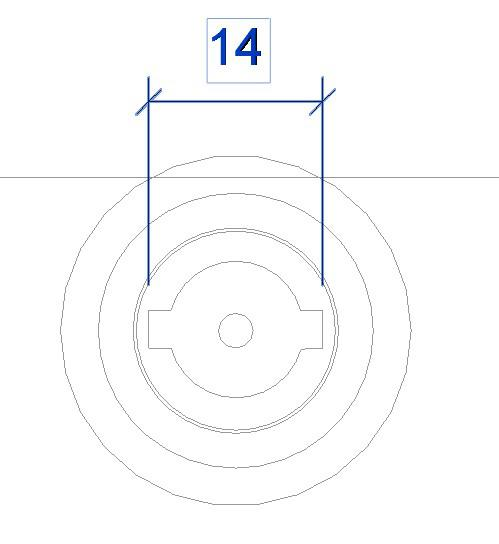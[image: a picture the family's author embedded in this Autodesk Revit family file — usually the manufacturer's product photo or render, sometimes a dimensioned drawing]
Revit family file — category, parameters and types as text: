
# Revit family: AquaMaster-Inverter-P_ENG-RFA-2022
name_source: partatom
category: Mechanické zařízení
units: mm (PartAtom-declared; Revit-internal decimal feet)

## family parameters
Bod výpočtu místnosti = Ne
Kóta kulaté spojky = Použít průměr
Nadpis OmniClass = Climate Control (HVAC)
Ořezat dutým tvarem při načtení = Ne
Sdílené = Ne
Typ dílu = Normální
Vždy vertikální = Ano
Zachovat orientaci poznámky = Ne
Založené na pracovní rovině = Ne
Číslo OmniClass = 23.75.00.00

## types (5) — shared parameters
CI_hot water – inlet = 1'' (OD)
CO_hot water – outlet = 1'' (OD)
MT_CI diameter = 28 mm  [stored 0.0918635 ft]
MT_CO diameter = 28 mm  [stored 0.0918635 ft]
MT_EC1 offset_X = 25 mm  [stored 0.082021 ft]
MT_active power = 0 W
MT_angle length_X = 406 mm  [stored 1.33202 ft]
MT_angle offset = 60 mm  [stored 0.19685 ft]
MT_apparent power = 0 VA
MT_case mat = MT_RAL7016
MT_case width = 526 mm  [stored 1.72572 ft]
MT_clearance back = 200 mm  [stored 0.656168 ft]
MT_clearance front = 600 mm
MT_cover front_X = 446 mm  [stored 1.46325 ft]
MT_cover top_X = 446 mm  [stored 1.46325 ft]
MT_frequency (Hz) = 50 Hz
MT_ground height = 30 mm  [stored 0.0984252 ft]
MT_pipe connector mat = MT_RGB-130-130-130
MT_pipe mat = MT_angle-corner
Popis = Ground-to-water heat pump (R290)
URL = https://www.mastertherm.eu
Výrobce = Master Therm
zero-valued in all types: Cena, MT_CosPhi, Výchozí výška

## per-type parameters (varying)
- AQ45IP: EI_brine – inlet=5/4'' (OD); EO_brine – outlet=5/4'' (OD); El. connection=2xPG16; 4xPG13.5; Komentáře k typům=COMPRESSOR: BLDC Inverter; 15 – 120 rps; oil – (HAF68D1U) – 2.0 l; max. op. current – 24 A; EVAPORATOR: PHE; AISI316; water flow (W/W) – 2.14 kg/s; min. flow – 1.61 kg/s; brine flow (B/W) – 1.04 kg/s; min. flow – 0.63 kg/s; temp. difference – 3 K; int. volume – 5.1 l; pump ext. head – 15 m; pump motor – 400 W; CONDENSER: PHE; AISI316; water flow – 0.7 kg/s; min. flow – 0.53 kg/s; temp. difference – 5 K; int. volume – 4.1 l; pump ext. head – 8.0 m; pump motor – 200 W; REFRIGERANT CIRCUIT: R290 (0.9 kg); AUX. HEATER (optional): není k dispozici; CONTROLS: controller – pCO5; EEV – yes; water probe – yes; mixing probe/output – yes (2x); SHW probe/output – yes; outdoor probe – yes; dynamic set point – yes; refrigerant probe – 2xPT; POWER SUPPLY: 3x400 V; 50 Hz; max. current – 25 A; DIMENSIONS: hot water, brine – 1", 5/4" (OD); 120x53x72 cm; 180 kg; LIMITS: max. water overpress. – 0.25 MPa; max. refr. overpress. – 3.1 MPa; brine min./max.: -5/+20 °C; water min./max.: 20/75 °C; MT_CI offset_X=73 mm  [stored 0.239501 ft]; MT_CO offset_X=173 mm  [stored 0.567585 ft]; MT_EC1 offset_Y=90 mm; MT_EC2 offset_X=25 mm  [stored 0.082021 ft]; MT_EC2 offset_Y=60 mm  [stored 0.19685 ft]; MT_EC3 offset_X=25 mm  [stored 0.082021 ft]; MT_EC3 offset_Y=30 mm  [stored 0.0984252 ft]; MT_EC4 offset_X=421 mm  [stored 1.38123 ft]; MT_EC4 offset_Y=90 mm; MT_EC5 offset_X=421 mm  [stored 1.38123 ft]; MT_EC5 offset_Y=60 mm  [stored 0.19685 ft]; MT_EC5-EC6_YES=Ano; MT_EC6 offset_X=421 mm  [stored 1.38123 ft]; MT_EC6 offset_Y=30 mm  [stored 0.0984252 ft]; MT_EI diameter=35 mm  [stored 0.114829 ft]; MT_EI offset_X=373 mm  [stored 1.22375 ft]; MT_EO diameter=35 mm  [stored 0.114829 ft]; MT_EO offset_X=273 mm  [stored 0.895669 ft]; MT_TYPE=45; MT_angle length_Y=596 mm; MT_angle length_Z=1080 mm; MT_case depth=716 mm; MT_case height=1200 mm; MT_center lock_YES=Ne; MT_clearance left=400 mm  [stored 1.31234 ft]; MT_clearance right=400 mm  [stored 1.31234 ft]; MT_clearance top=1800 mm  [stored 5.90551 ft]; MT_cover front_Y=1120 mm; MT_cover side_X=636 mm; MT_cover side_Y=1120 mm; MT_cover top_Y=636 mm; MT_max. current, incl. aux. heater (A)=25 A; MT_pipe connector angle=0.00°; MT_pipe connector offset=486 mm; MT_pipe connector_X=446 mm  [stored 1.46325 ft]; MT_pipe connector_Y=120 mm  [stored 0.393701 ft]; MT_pivot offset=0 mm  [stored 0 ft]; MT_vent grille_YES=Ne; MT_voltage (V)=400 V; MT_weight (kg)=180; Model=AquaMaster 45 Inverter P
- AQ17IP: EI_brine – inlet=1'' (OD); EO_brine – outlet=1'' (OD); El. connection=4xPG16; Komentáře k typům=COMPRESSOR: BLDC Inverter; 20 – 60 rps; oil – (RFL68EP) – 0.74 l; max. op. current – 12 A; EVAPORATOR: PHE; AISI316; water flow (W/W) – 0.22 kg/s; min. flow – 0.17 kg/s; brine flow (B/W) – 0.18 kg/s; min. flow – 0.11 kg/s; temp. difference – 3 K; int. volume – 2.0 l; pump ext. head – 6.0 m; pump motor – 70 W; CONDENSER: PHE; AISI316; water flow – 0.12 kg/s; min. flow – 0.06 kg/s; temp. difference – 5 K; int. volume – 2.0 l; pump ext. head – 5.0 m; pump motor – 70 W; REFRIGERANT CIRCUIT: R290 (0.152 kg); AUX. HEATER (optional): not available; CONTROLS: controller – pCO5; EEV – yes; water probe – yes; mixing probe/output – yes (2x); SHW probe/output – yes; outdoor probe – yes; dynamic set point – yes; refrigerant probe – 2xPT; POWER SUPPLY: 1x230 V; 50 Hz; max. current – 16 A; DIMENSIONS: hot water, brine – 1", 1" (OD); 84x53x53 cm; 75 kg; LIMITS: max. water overpress. – 0.25 MPa; max. refr. overpress. – 3.1 MPa; brine min./max.: -5/+20 °C; water min./max.: 20/75 °C; MT_CI offset_X=430 mm; MT_CO offset_X=700 mm; MT_EC1 offset_Y=500 mm  [stored 1.64042 ft]; MT_EC2 offset_X=55 mm  [stored 0.180446 ft]; MT_EC2 offset_Y=500 mm  [stored 1.64042 ft]; MT_EC3 offset_X=85 mm  [stored 0.278871 ft]; MT_EC3 offset_Y=500 mm  [stored 1.64042 ft]; MT_EC4 offset_X=115 mm; MT_EC4 offset_Y=500 mm  [stored 1.64042 ft]; MT_EC5 offset_X=115 mm; MT_EC5 offset_Y=500 mm  [stored 1.64042 ft]; MT_EC5-EC6_YES=Ne; MT_EC6 offset_X=115 mm; MT_EC6 offset_Y=500 mm  [stored 1.64042 ft]; MT_EI diameter=28 mm  [stored 0.0918635 ft]; MT_EI offset_X=330 mm; MT_EO diameter=28 mm  [stored 0.0918635 ft]; MT_EO offset_X=60 mm  [stored 0.19685 ft]; MT_TYPE=17; MT_angle length_Y=406 mm  [stored 1.33202 ft]; MT_angle length_Z=720 mm  [stored 2.3622 ft]; MT_case depth=526 mm  [stored 1.72572 ft]; MT_case height=840 mm  [stored 2.75591 ft]; MT_center lock_YES=Ano; MT_clearance left=200 mm  [stored 0.656168 ft]; MT_clearance right=600 mm; MT_clearance top=1440 mm  [stored 4.72441 ft]; MT_cover front_Y=760 mm  [stored 2.49344 ft]; MT_cover side_X=446 mm  [stored 1.46325 ft]; MT_cover side_Y=760 mm  [stored 2.49344 ft]; MT_cover top_Y=446 mm  [stored 1.46325 ft]; MT_max. current, incl. aux. heater (A)=16 A; MT_pipe connector angle=90.00°; MT_pipe connector offset=800 mm; MT_pipe connector_X=760 mm  [stored 2.49344 ft]; MT_pipe connector_Y=85 mm  [stored 0.278871 ft]; MT_pivot offset=526 mm  [stored 1.72572 ft]; MT_vent grille_YES=Ano; MT_voltage (V)=230 V; MT_weight (kg)=75; Model=AquaMaster 17 Inverter P
- AQ22IP: EI_brine – inlet=1'' (OD); EO_brine – outlet=1'' (OD); El. connection=4xPG16; Komentáře k typům=COMPRESSOR: BLDC Inverter; 20 – 90 rps; oil – (RFL68EP) – 0.74 l; max. op. current – 12 A; EVAPORATOR: PHE; AISI316; water flow (W/W) – 0.46 kg/s; min. flow – 0.35 kg/s; brine flow (B/W) – 0.36 kg/s; min. flow – 0.21 kg/s; temp. difference – 3 K; int. volume – 2.0 l; pump ext. head – 4.5 m; pump motor – 70 W; CONDENSER: PHE; AISI316; water flow – 0.25 kg/s; min. flow – 0.13 kg/s; temp. difference – 5 K; int. volume – 2.0 l; pump ext. head – 7.0 m; pump motor – 70 W; REFRIGERANT CIRCUIT: R290 (0.220 kg); AUX. HEATER (optional): není k dispozici; CONTROLS: controller – pCO5; EEV – yes; water probe – yes; mixing probe/output – yes (2x); SHW probe/output – yes; outdoor probe – yes; dynamic set point – yes; refrigerant probe – 2xPT; POWER SUPPLY: 1x230 V; 50 Hz; max. current – 20 A; DIMENSIONS: hot water, brine – 1", 1" (OD); 84x53x53 cm; 80 kg; LIMITS: max. water overpress. – 0.25 MPa; max. refr. overpress. – 3.1 MPa; brine min./max.: -5/+20 °C; water min./max.: 20/75 °C; MT_CI offset_X=430 mm; MT_CO offset_X=700 mm; MT_EC1 offset_Y=500 mm  [stored 1.64042 ft]; MT_EC2 offset_X=55 mm  [stored 0.180446 ft]; MT_EC2 offset_Y=500 mm  [stored 1.64042 ft]; MT_EC3 offset_X=85 mm  [stored 0.278871 ft]; MT_EC3 offset_Y=500 mm  [stored 1.64042 ft]; MT_EC4 offset_X=115 mm; MT_EC4 offset_Y=500 mm  [stored 1.64042 ft]; MT_EC5 offset_X=115 mm; MT_EC5 offset_Y=500 mm  [stored 1.64042 ft]; MT_EC5-EC6_YES=Ne; MT_EC6 offset_X=115 mm; MT_EC6 offset_Y=500 mm  [stored 1.64042 ft]; MT_EI diameter=28 mm  [stored 0.0918635 ft]; MT_EI offset_X=330 mm; MT_EO diameter=28 mm  [stored 0.0918635 ft]; MT_EO offset_X=60 mm  [stored 0.19685 ft]; MT_TYPE=22; MT_angle length_Y=406 mm  [stored 1.33202 ft]; MT_angle length_Z=720 mm  [stored 2.3622 ft]; MT_case depth=526 mm  [stored 1.72572 ft]; MT_case height=840 mm  [stored 2.75591 ft]; MT_center lock_YES=Ano; MT_clearance left=200 mm  [stored 0.656168 ft]; MT_clearance right=600 mm; MT_clearance top=1440 mm  [stored 4.72441 ft]; MT_cover front_Y=760 mm  [stored 2.49344 ft]; MT_cover side_X=446 mm  [stored 1.46325 ft]; MT_cover side_Y=760 mm  [stored 2.49344 ft]; MT_cover top_Y=446 mm  [stored 1.46325 ft]; MT_max. current, incl. aux. heater (A)=20 A; MT_pipe connector angle=90.00°; MT_pipe connector offset=800 mm; MT_pipe connector_X=760 mm  [stored 2.49344 ft]; MT_pipe connector_Y=85 mm  [stored 0.278871 ft]; MT_pivot offset=526 mm  [stored 1.72572 ft]; MT_vent grille_YES=Ano; MT_voltage (V)=230 V; MT_weight (kg)=80; Model=AquaMaster 22 Inverter P
- AQ30IP: EI_brine – inlet=1'' (OD); EO_brine – outlet=1'' (OD); El. connection=2xPG16; 4xPG13.5; Komentáře k typům=COMPRESSOR: BLDC Inverter; 15 – 110 rps; oil – (PZ68S) – 0.75 l; max. op. current – ; EVAPORATOR: PHE; AISI316; water flow (W/W) – 0.99 kg/s; min. flow – 0.74 kg/s; brine flow (B/W) – 0.48 kg/s; min. flow – 0.29 kg/s; temp. difference – 3 K; int. volume – 3.8 l; pump ext. head – 5.5 m; pump motor – 70 W; CONDENSER: PHE; AISI316; water flow – 0.37 kg/s; min. flow – 0.25 kg/s; temp. difference – 5 K; int. volume – 4.0 l; pump ext. head – 6.5 m; pump motor – 70 W; REFRIGERANT CIRCUIT: R290 (0.7 kg); AUX. HEATER (optional): není k dispozici; CONTROLS: controller – pCO5; EEV – yes; water probe – yes; mixing probe/output – yes (2x); SHW probe/output – yes; outdoor probe – yes; dynamic set point – yes; refrigerant probe – 2xPT; POWER SUPPLY: 1x230 V; 50 Hz; max. current – 25 A; DIMENSIONS: hot water, brine – 1", 1" (OD); 120x56x72 cm; 165 kg; LIMITS: max. water overpress. – 0.25 MPa; max. refr. overpress. – 2.9 MPa; brine min./max.: -5/+20 °C; water min./max.: 20/75 °C; MT_CI offset_X=73 mm  [stored 0.239501 ft]; MT_CO offset_X=173 mm  [stored 0.567585 ft]; MT_EC1 offset_Y=90 mm; MT_EC2 offset_X=25 mm  [stored 0.082021 ft]; MT_EC2 offset_Y=60 mm  [stored 0.19685 ft]; MT_EC3 offset_X=25 mm  [stored 0.082021 ft]; MT_EC3 offset_Y=30 mm  [stored 0.0984252 ft]; MT_EC4 offset_X=421 mm  [stored 1.38123 ft]; MT_EC4 offset_Y=90 mm; MT_EC5 offset_X=421 mm  [stored 1.38123 ft]; MT_EC5 offset_Y=60 mm  [stored 0.19685 ft]; MT_EC5-EC6_YES=Ano; MT_EC6 offset_X=421 mm  [stored 1.38123 ft]; MT_EC6 offset_Y=30 mm  [stored 0.0984252 ft]; MT_EI diameter=28 mm  [stored 0.0918635 ft]; MT_EI offset_X=373 mm  [stored 1.22375 ft]; MT_EO diameter=28 mm  [stored 0.0918635 ft]; MT_EO offset_X=273 mm  [stored 0.895669 ft]; MT_TYPE=30; MT_angle length_Y=596 mm; MT_angle length_Z=1080 mm; MT_case depth=716 mm; MT_case height=1200 mm; MT_center lock_YES=Ne; MT_clearance left=400 mm  [stored 1.31234 ft]; MT_clearance right=400 mm  [stored 1.31234 ft]; MT_clearance top=1800 mm  [stored 5.90551 ft]; MT_cover front_Y=1120 mm; MT_cover side_X=636 mm; MT_cover side_Y=1120 mm; MT_cover top_Y=636 mm; MT_max. current, incl. aux. heater (A)=25 A; MT_pipe connector angle=0.00°; MT_pipe connector offset=486 mm; MT_pipe connector_X=446 mm  [stored 1.46325 ft]; MT_pipe connector_Y=120 mm  [stored 0.393701 ft]; MT_pivot offset=0 mm  [stored 0 ft]; MT_vent grille_YES=Ne; MT_voltage (V)=230 V; MT_weight (kg)=165; Model=AquaMaster 30 Inverter P
- AQ37IP: EI_brine – inlet=1'' (OD); EO_brine – outlet=1'' (OD); El. connection=2xPG16; 4xPG13.5; Komentáře k typům=COMPRESSOR: BLDC Inverter; 15 – 100 rps; oil – (PZ68S) – 0.9 l; max. op. current – ; EVAPORATOR: PHE; AISI316; water flow (W/W) – 1.54 kg/s; min. flow – 1.16 kg/s; brine flow (B/W) – 0.77 kg/s; min. flow – 0.46 kg/s; temp. difference – 3 K; int. volume – 3.8 l; pump ext. head – 7.5 m; pump motor – 200 W; CONDENSER: PHE; AISI316; water flow – 0.6 kg/s; min. flow – 0.4 kg/s; temp. difference – 5 K; int. volume – 4.0 l; pump ext. head – 4.5 m; pump motor – 70 W; REFRIGERANT CIRCUIT: R290 (0.9 kg); AUX. HEATER (optional): není k dispozici; CONTROLS: controller – pCO5; EEV – yes; water probe – yes; mixing probe/output – yes (2x); SHW probe/output – yes; outdoor probe – yes; dynamic set point – yes; refrigerant probe – 2xPT; POWER SUPPLY: 3x400 V; 50 Hz; max. current – 20 A; DIMENSIONS: hot water, brine – 1", 1" (OD); 120x56x72 cm; 180 kg; LIMITS: max. water overpress. – 0.25 MPa; max. refr. overpress. – 2.9 MPa; brine min./max.: -5/+20 °C; water min./max.: 20/75 °C; MT_CI offset_X=73 mm  [stored 0.239501 ft]; MT_CO offset_X=173 mm  [stored 0.567585 ft]; MT_EC1 offset_Y=90 mm; MT_EC2 offset_X=25 mm  [stored 0.082021 ft]; MT_EC2 offset_Y=60 mm  [stored 0.19685 ft]; MT_EC3 offset_X=25 mm  [stored 0.082021 ft]; MT_EC3 offset_Y=30 mm  [stored 0.0984252 ft]; MT_EC4 offset_X=421 mm  [stored 1.38123 ft]; MT_EC4 offset_Y=90 mm; MT_EC5 offset_X=421 mm  [stored 1.38123 ft]; MT_EC5 offset_Y=60 mm  [stored 0.19685 ft]; MT_EC5-EC6_YES=Ano; MT_EC6 offset_X=421 mm  [stored 1.38123 ft]; MT_EC6 offset_Y=30 mm  [stored 0.0984252 ft]; MT_EI diameter=28 mm  [stored 0.0918635 ft]; MT_EI offset_X=373 mm  [stored 1.22375 ft]; MT_EO diameter=28 mm  [stored 0.0918635 ft]; MT_EO offset_X=273 mm  [stored 0.895669 ft]; MT_TYPE=37; MT_angle length_Y=596 mm; MT_angle length_Z=1080 mm; MT_case depth=716 mm; MT_case height=1200 mm; MT_center lock_YES=Ne; MT_clearance left=400 mm  [stored 1.31234 ft]; MT_clearance right=400 mm  [stored 1.31234 ft]; MT_clearance top=1800 mm  [stored 5.90551 ft]; MT_cover front_Y=1120 mm; MT_cover side_X=636 mm; MT_cover side_Y=1120 mm; MT_cover top_Y=636 mm; MT_max. current, incl. aux. heater (A)=20 A; MT_pipe connector angle=0.00°; MT_pipe connector offset=486 mm; MT_pipe connector_X=446 mm  [stored 1.46325 ft]; MT_pipe connector_Y=120 mm  [stored 0.393701 ft]; MT_pivot offset=0 mm  [stored 0 ft]; MT_vent grille_YES=Ne; MT_voltage (V)=400 V; MT_weight (kg)=180; Model=AquaMaster 37 Inverter P

note: [stored X ft] marks values corroborated as IEEE doubles in the binary element streams (Revit-internal decimal feet)
